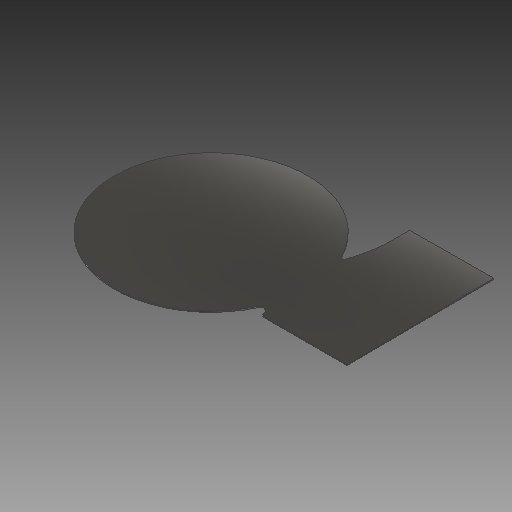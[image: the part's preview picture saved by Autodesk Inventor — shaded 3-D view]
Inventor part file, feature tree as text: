
AUTODESK INVENTOR PART (.ipt)
format: ipt  version: 2018 (Build 220112000, 112)  size: 113,152 bytes
history: native  units: mm
features: other x3, sketch x1
ambient origin geometry x8: Origin, YZ Plane, XZ Plane, XY Plane, X Axis, Y Axis, Z Axis, Center Point
bodies: Volumenkörper1 (feature_tree)
feature tree (4):
  other  "Solarpanel.ipt"
  other  "Volumenkörper1::Solarpanel.ipt"
  other  "Bezeichnung1"
  sketch  "Skizze6"  dims[d0=10.0mm]
